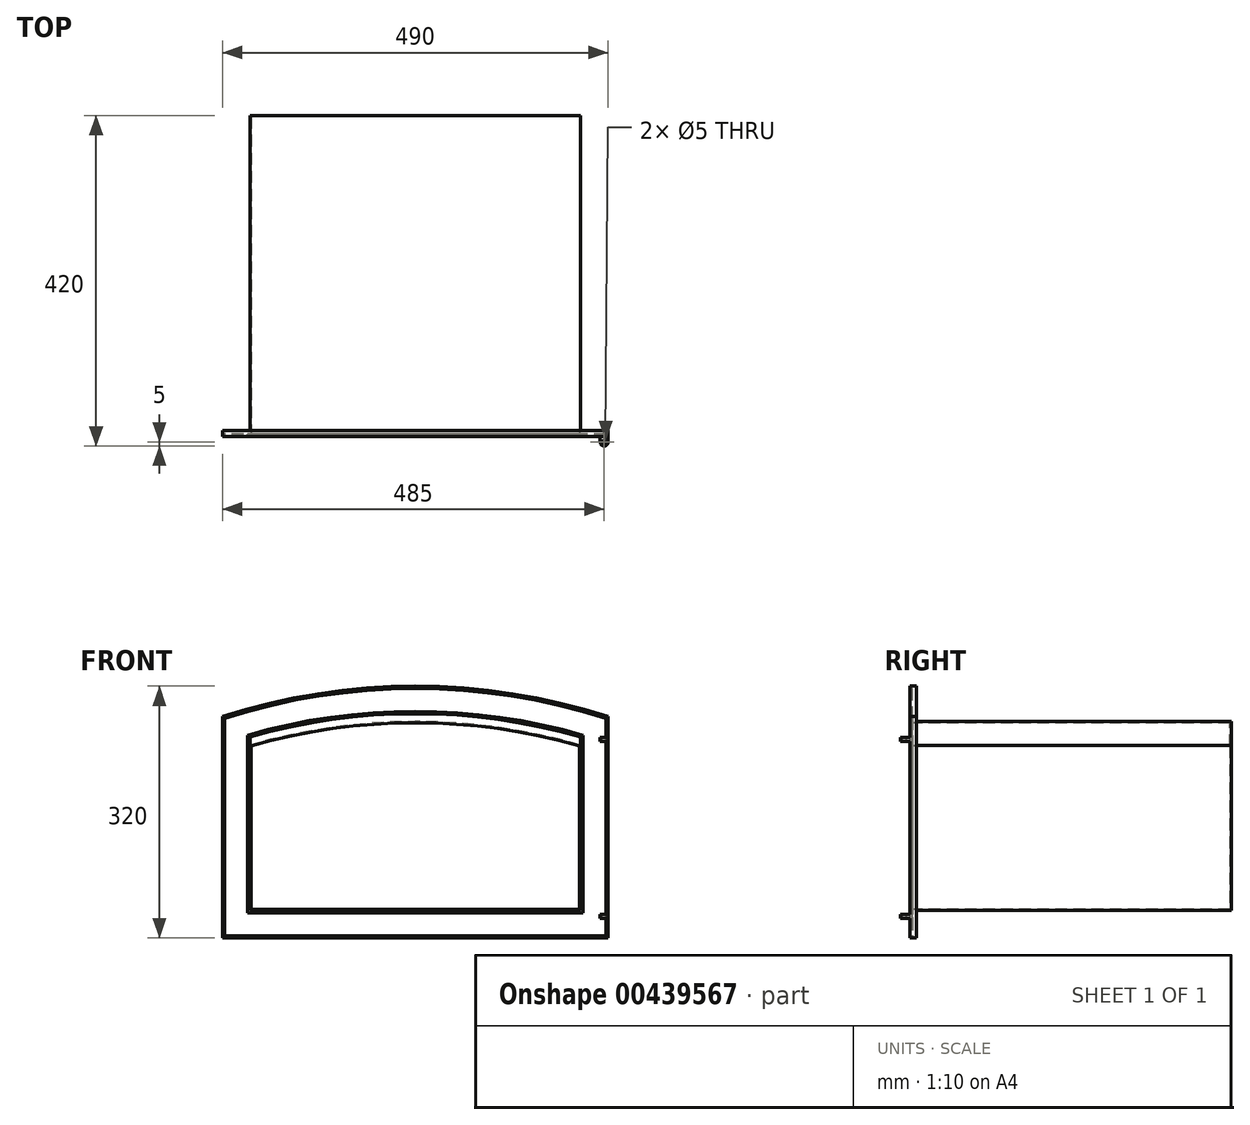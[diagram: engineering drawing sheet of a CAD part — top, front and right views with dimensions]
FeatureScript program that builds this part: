
annotation { "Feature Type Name" : "Feature", "Feature Type Description" : "" }
export const myFeature = defineFeature(function(context is Context, id is Id, definition is map)
    precondition{}
    {
        {
            var Q0;
            Q0=qCreatedBy(makeId("Front.planeOp"),FACE);
            var sketch = newSketch(context, id + "F0", { "sketchPlane" : qUnion([Q0])});
            skLineSegment(sketch, "E0.bottom", {"start": v(210, 105) * mm, "end": v(-210, 105) * mm, "construction": true});
            skLineSegment(sketch, "E0.top", {"start": v(210, -105) * mm, "end": v(-210, -105) * mm});
            skLineSegment(sketch, "E0.left", {"start": v(210, 105) * mm, "end": v(210, -105) * mm});
            skLineSegment(sketch, "E0.right", {"start": v(-210, 105) * mm, "end": v(-210, -105) * mm});
            skPoint(sketch, "E0.middle", {"position": v(0, 0) * mm});
            skLineSegment(sketch, "E1", {"start": v(0, -105) * mm, "end": v(0, 135) * mm, "construction": true});
            skPoint(sketch, "E1.endSnap0", {"position": v(0, 105) * mm});
            skArc(sketch, "E2", {"start": v(210, 105) * mm, "mid": v(0, 135) * mm, "end": v(-210, 105) * mm});
            skLineSegment(sketch, "E3.0", {"start": v(-245, 141.3) * mm, "end": v(-245, -140) * mm});
            skLineSegment(sketch, "E4.0", {"start": v(245, 141.3) * mm, "end": v(245, -140) * mm});
            skLineSegment(sketch, "E5.0", {"start": v(245, -140) * mm, "end": v(-245, -140) * mm});
            skArc(sketch, "E6.0", {"start": v(245, 141.3) * mm, "mid": v(0, 180) * mm, "end": v(-245, 141.3) * mm});
            skSolve(sketch);
        }
        {
            var Q0;
            Q0=makeQuery(id+"F0.imprint","IMPRINT",FACE,{"disambiguationData":[TD([[makeQuery(id+"F0.imprint","IMPRINT",EDGE,{"derivedFrom":sQuery(id+"F0.wireOp",EDGE,"E0.top")}),-1.0]])]});
            extrude(context, id + "F1", {"entities" : qUnion([Q0]), "oppositeDirection" : true, "depth" : 405 * mm});
        }
        {
            var Q0;
            Q0=makeQuery(id+"F1.opExtrude","CAP_FACE",FACE,{"disambiguationData":[OSD([sQuery(id+"F0.wireOp",EDGE,"E0.top"),sQuery(id+"F0.wireOp",EDGE,"E0.left"),sQuery(id+"F0.wireOp",EDGE,"E0.right"),sQuery(id+"F0.wireOp",EDGE,"E2")])],"isStart":true});
            shell(context, id + "F2", {"entities" : qUnion([Q0]), "thickness" : 1.5 * mm});
        }
        {
            var Q0;
            Q0=makeQuery(id+"F0.imprint","IMPRINT",FACE,{"disambiguationData":[TD([[makeQuery(id+"F0.imprint","IMPRINT",EDGE,{"derivedFrom":sQuery(id+"F0.wireOp",EDGE,"E0.top")}),1.0]])]});
            extrude(context, id + "F3", {"entities" : qUnion([Q0]), "operationType" : NewBodyOperationType.ADD, "oppositeDirection" : true, "depth" : 5 * mm});
        }
        {
            var Q0;
            Q0=makeQuery(id+"F0.imprint","IMPRINT",FACE,{"disambiguationData":[TD([[makeQuery(id+"F0.imprint","IMPRINT",EDGE,{"derivedFrom":sQuery(id+"F0.wireOp",EDGE,"E0.top")}),1.0]])]});
            var sketch = newSketch(context, id + "F4", { "sketchPlane" : qUnion([Q0])});
            skArc(sketch, "E7.0", {"start": v(245, 141.3) * mm, "mid": v(0, 180) * mm, "end": v(-245, 141.3) * mm});
            skLineSegment(sketch, "E8.0", {"start": v(-245, 141.3) * mm, "end": v(-245, -140) * mm});
            skLineSegment(sketch, "E9.0", {"start": v(245, -140) * mm, "end": v(-245, -140) * mm});
            skLineSegment(sketch, "E10.0", {"start": v(245, 141.3) * mm, "end": v(245, -140) * mm});
            skLineSegment(sketch, "E11.0", {"start": v(210, 115.41) * mm, "end": v(210, -105) * mm});
            skArc(sketch, "E12.0", {"start": v(210, 105) * mm, "mid": v(0, 135) * mm, "end": v(-210, 105) * mm, "construction": true});
            skLineSegment(sketch, "E13.0", {"start": v(-210, 115.41) * mm, "end": v(-210, -105) * mm});
            skLineSegment(sketch, "E14.0", {"start": v(210, -105) * mm, "end": v(-210, -105) * mm});
            skArc(sketch, "E15.0", {"start": v(210, 115.41) * mm, "mid": v(0, 145) * mm, "end": v(-210, 115.41) * mm});
            skPoint(sketch, "E16.orphan", {"position": v(-210, 105) * mm});
            skPoint(sketch, "E17.orphan", {"position": v(210, 105) * mm});
            skLineSegment(sketch, "E18.0", {"start": v(-242, 139.12) * mm, "end": v(-242, -137) * mm});
            skArc(sketch, "E18.1", {"start": v(242, 139.12) * mm, "mid": v(0, 177) * mm, "end": v(-242, 139.12) * mm});
            skLineSegment(sketch, "E18.2", {"start": v(242, 139.12) * mm, "end": v(242, -137) * mm});
            skLineSegment(sketch, "E18.3", {"start": v(242, -137) * mm, "end": v(-242, -137) * mm});
            skLineSegment(sketch, "E19.0", {"start": v(-213, 117.67) * mm, "end": v(-213, -108) * mm});
            skArc(sketch, "E19.1", {"start": v(213, 117.67) * mm, "mid": v(0, 148) * mm, "end": v(-213, 117.67) * mm});
            skLineSegment(sketch, "E19.2", {"start": v(213, 117.67) * mm, "end": v(213, -108) * mm});
            skLineSegment(sketch, "E19.3", {"start": v(213, -108) * mm, "end": v(-213, -108) * mm});
            skSolve(sketch);
        }
        {
            var Q0;
            Q0=makeQuery(id+"F4.imprint","IMPRINT",FACE,{"disambiguationData":[TD([[makeQuery(id+"F4.imprint","IMPRINT",EDGE,{"derivedFrom":sQuery(id+"F4.wireOp",EDGE,"E7.0")}),1.0]])]});
            extrude(context, id + "F5", {"entities" : qUnion([Q0]), "operationType" : NewBodyOperationType.ADD, "depth" : 3 * mm});
        }
        {
            var Q0;
            {var subQ0=sQuery(id+"F4.wireOp",EDGE,"E14.0");Q0=makeQuery(id+"F4.imprint","IMPRINT",FACE,{"disambiguationData":[TD([[makeQuery(id+"F4.imprint","IMPRINT",EDGE,{"derivedFrom":subQ0}),1.0]])]});}
            extrude(context, id + "F6", {"entities" : qUnion([Q0]), "operationType" : NewBodyOperationType.ADD, "depth" : 2 * mm});
        }
        {
            var Q0;
            Q0=makeQuery(id+"F4.imprint","IMPRINT",FACE,{"disambiguationData":[TD([[makeQuery(id+"F4.imprint","IMPRINT",EDGE,{"derivedFrom":sQuery(id+"F4.wireOp",EDGE,"E18.0")}),1.0]])]});
            var sketch = newSketch(context, id + "F7", { "sketchPlane" : qUnion([Q0])});
            skLineSegment(sketch, "E20.0", {"start": v(245, 141.3) * mm, "end": v(245, -140) * mm, "construction": true});
            skLineSegment(sketch, "E21.bottom", {"start": v(245, 115) * mm, "end": v(235, 115) * mm});
            skLineSegment(sketch, "E21.top", {"start": v(245, 110) * mm, "end": v(235, 110) * mm});
            skLineSegment(sketch, "E21.left", {"start": v(245, 115) * mm, "end": v(245, 110) * mm});
            skLineSegment(sketch, "E21.right", {"start": v(235, 115) * mm, "end": v(235, 110) * mm});
            skLineSegment(sketch, "E22.bottom", {"start": v(245, -115) * mm, "end": v(235, -115) * mm});
            skLineSegment(sketch, "E22.top", {"start": v(245, -110) * mm, "end": v(235, -110) * mm});
            skLineSegment(sketch, "E22.left", {"start": v(245, -115) * mm, "end": v(245, -110) * mm});
            skLineSegment(sketch, "E22.right", {"start": v(235, -115) * mm, "end": v(235, -110) * mm});
            skSolve(sketch);
        }
        {
            var Q0;
            Q0 = qSketchRegion(id + "F7", true);
            extrude(context, id + "F8", {"entities" : qUnion([Q0]), "operationType" : NewBodyOperationType.ADD, "depth" : 15 * mm});
        }
        {
            var Q0;
            Q0=makeQuery(id+"F8.opExtrude","CAP_EDGE",EDGE,{"disambiguationData":[OSD([sQuery(id+"F7.wireOp",EDGE,"E21.left")])],"isStart":false});
            var Q1;
            Q1=makeQuery(id+"F8.opExtrude","CAP_EDGE",EDGE,{"disambiguationData":[OSD([sQuery(id+"F7.wireOp",EDGE,"E21.right")])],"isStart":false});
            var Q2;
            Q2=makeQuery(id+"F8.opExtrude","CAP_EDGE",EDGE,{"disambiguationData":[OSD([sQuery(id+"F7.wireOp",EDGE,"E22.left")])],"isStart":false});
            var Q3;
            Q3=makeQuery(id+"F8.opExtrude","CAP_EDGE",EDGE,{"disambiguationData":[OSD([sQuery(id+"F7.wireOp",EDGE,"E22.right")])],"isStart":false});
            fillet(context, id + "F9", {"entities" : qUnion([Q0, Q1, Q2, Q3]), "radius" : 5 * mm, "tangentPropagation" : true, "allowEdgeOverflow" : false});
        }
        {
            var Q0;
            Q0=makeQuery(id+"F8.opExtrude","SWEPT_FACE",FACE,{"disambiguationData":[OSD([sQuery(id+"F7.wireOp",EDGE,"E21.bottom")])]});
            var sketch = newSketch(context, id + "F10", { "sketchPlane" : qUnion([Q0])});
            skPoint(sketch, "E23", {"position": v(240, -10) * mm});
            skSolve(sketch);
        }
        {
            var Q0;
            Q0=sQuery(id+"F10.wireOp",VERTEX,"E23");
            var Q1;
            Q1=makeQuery(id+"F1.opExtrude","SWEPT_BODY",BODY,{"disambiguationData":[OSD([sQuery(id+"F0.wireOp",EDGE,"E0.top"),sQuery(id+"F0.wireOp",EDGE,"E0.left"),sQuery(id+"F0.wireOp",EDGE,"E0.right"),sQuery(id+"F0.wireOp",EDGE,"E2")])]});
            hole(context, id + "F11", {"style" : HoleStyle.SIMPLE, "endStyle" : HoleEndStyle.THROUGH, "holeDiameter" : 5 * mm, "isTappedThrough" : true, "tappedDepth" : 12 * mm, "tapClearance" : 3, "locations" : qUnion([Q0]), "scope" : qUnion([Q1])});
        }
    });
